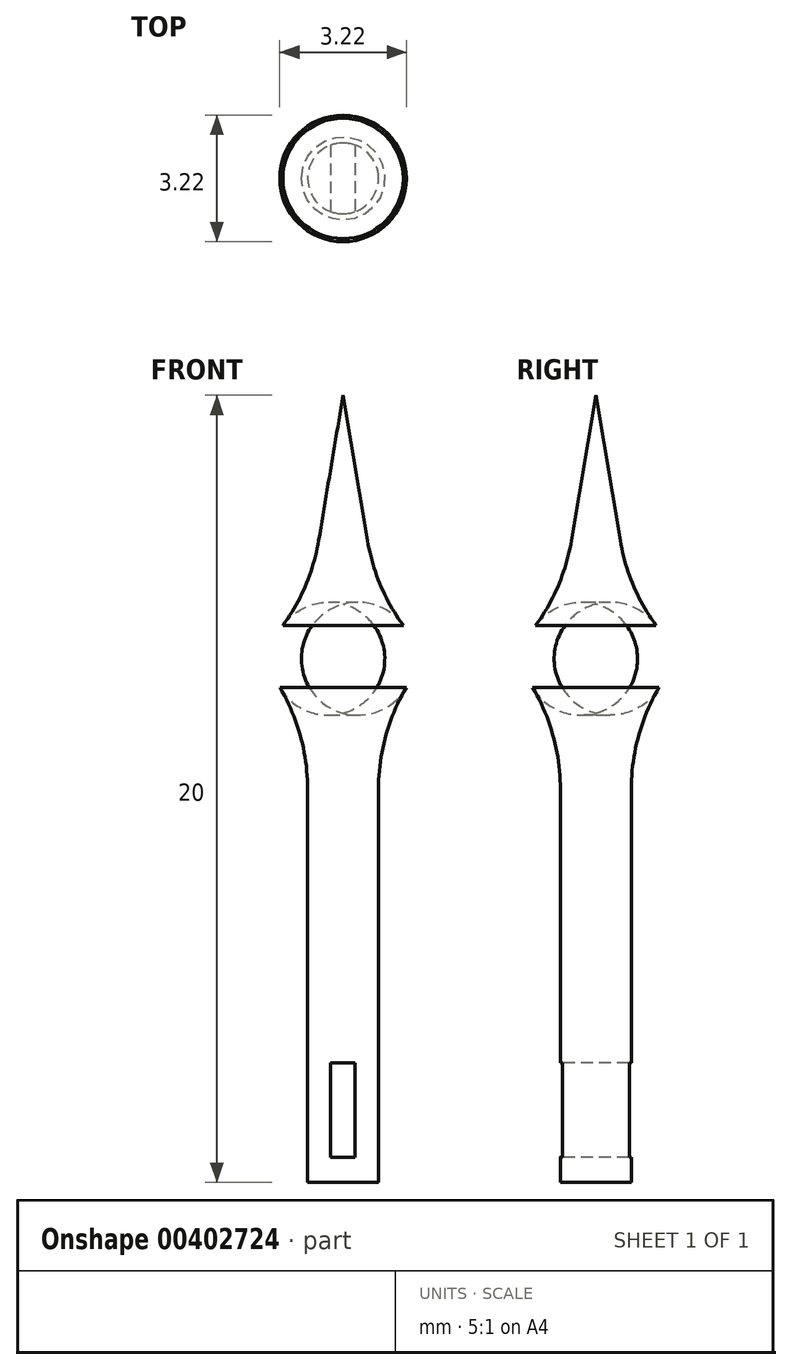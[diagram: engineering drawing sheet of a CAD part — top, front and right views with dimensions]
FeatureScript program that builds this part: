
annotation { "Feature Type Name" : "Feature", "Feature Type Description" : "" }
export const myFeature = defineFeature(function(context is Context, id is Id, definition is map)
    precondition{}
    {
        {
            var Q0;
            Q0=qCreatedBy(makeId("Front.planeOp"),FACE);
            var sketch = newSketch(context, id + "F0", { "sketchPlane" : qUnion([Q0])});
            skLineSegment(sketch, "E0", {"start": v(0.99, 5.36) * mm, "end": v(1.89, 0) * mm});
            skArc(sketch, "E1", {"start": v(1.89, -2.67) * mm, "mid": v(2.8, -1.33) * mm, "end": v(1.89, 0) * mm});
            skLineSegment(sketch, "E2", {"start": v(1.89, -2.67) * mm, "end": v(1.89, -14.64) * mm});
            skLineSegment(sketch, "E3", {"start": v(0.99, 5.36) * mm, "end": v(0.99, -14.64) * mm});
            skLineSegment(sketch, "E4", {"start": v(0.99, -14.64) * mm, "end": v(1.89, -14.64) * mm});
            skSolve(sketch);
        }
        {
            var Q0;
            Q0 = qSketchRegion(id + "F0", true);
            var Q1;
            Q1=sQuery(id+"F0.wireOp",EDGE,"E3");
            revolve(context, id + "F1", {"entities" : qUnion([Q0]), "axis" : qUnion([Q1]), "revolveType" : RevolveType.FULL});
        }
        {
            var Q0;
            Q0=qCreatedBy(makeId("Front.planeOp"),FACE);
            var sketch = newSketch(context, id + "F2", { "sketchPlane" : qUnion([Q0])});
            skLineSegment(sketch, "E5.bottom", {"start": v(1.29, -14) * mm, "end": v(0.66, -14) * mm});
            skLineSegment(sketch, "E5.top", {"start": v(1.29, -11.6) * mm, "end": v(0.66, -11.6) * mm});
            skLineSegment(sketch, "E5.left", {"start": v(1.29, -14) * mm, "end": v(1.29, -11.6) * mm});
            skLineSegment(sketch, "E5.right", {"start": v(0.66, -14) * mm, "end": v(0.66, -11.6) * mm});
            skSolve(sketch);
        }
        {
            var Q0;
            Q0 = qSketchRegion(id + "F2", true);
            extrude(context, id + "F3", {"entities" : qUnion([Q0]), "operationType" : NewBodyOperationType.REMOVE, "endBound" : BoundingType.SYMMETRIC, "oppositeDirection" : true, "depth" : 25.4 * mm});
        }
        {
            var Q0;
            Q0=makeQuery(id+"F1.opRevolve","SWEPT_EDGE",EDGE,{"disambiguationData":[OSD([sQuery(id+"F0.wireOp",EDGE,"E1"),sQuery(id+"F0.wireOp",EDGE,"E2")])]});
            var Q1;
            Q1=makeQuery(id+"F1.opRevolve","SWEPT_EDGE",EDGE,{"disambiguationData":[OSD([sQuery(id+"F0.wireOp",EDGE,"E0"),sQuery(id+"F0.wireOp",EDGE,"E1")])]});
            fillet(context, id + "F4", {"entities" : qUnion([Q0, Q1]), "radius" : 5.08 * mm, "tangentPropagation" : true, "allowEdgeOverflow" : false});
        }
    });
